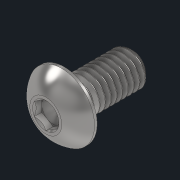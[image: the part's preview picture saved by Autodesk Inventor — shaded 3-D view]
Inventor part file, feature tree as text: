
AUTODESK INVENTOR PART (.ipt)
format: ipt  version: 2021 (Build 250183000, 183)  size: 530,432 bytes
history: native  units: in
note: dims shown in document units (in); Inventor stores cm internally (conversion verified against a paired STEP export)
features: revolve x1
ambient origin geometry x8: Origin, YZ Plane, XZ Plane, XY Plane, X Axis, Y Axis, Z Axis, Center Point
bodies: Solid1 (feature_tree)
feature tree (1):
  revolve  "Revolve2"  [1 undecoded]
note: 1 required parameter value undecoded (feature->parameter linkage not recoverable at this tier; creation-order binding heuristic only, values carry confidence <= 0.55)
